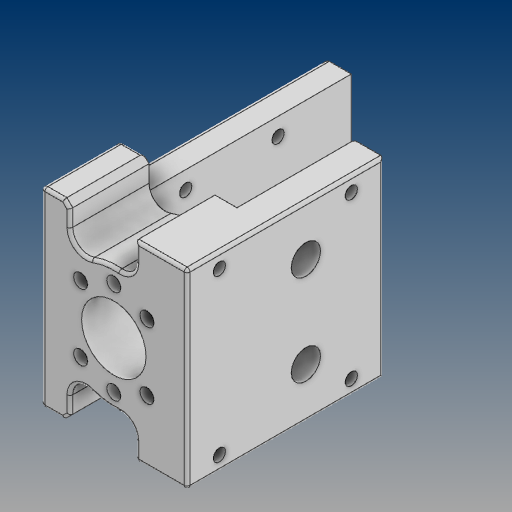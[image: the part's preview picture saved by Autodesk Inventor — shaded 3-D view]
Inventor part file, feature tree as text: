
AUTODESK INVENTOR PART (.ipt)
format: ipt  version: 2021 (Build 250183000, 183)  size: 435,200 bytes
history: native  units: mm
features: extrude x10, sketch x9, projected_geometry x9, reference x6, other x6, fillet x5, plane x1, mirror x1, chamfer x1
ambient origin geometry x8: Origin, YZ Plane, XZ Plane, XY Plane, X Axis, Y Axis, Z Axis, Center Point
bodies: Solid1 (feature_tree)
feature tree (48):
  sketch  "Sketch1"  dims[d0=30.0mm d1=21.0mm]
  plane  "Work Plane1"
  extrude  "Extrusion1"  Depth=21.0mm
  extrude  "Extrusion2"  Depth=30.0mm
  extrude  "Extrusion3"  Depth=15.0mm
  extrude  "Extrusion4"  Depth=10.0mm
  mirror  "Mirror1"
  extrude  "Extrusion5"  Depth=31.0mm
  fillet  "Fillet1"  Radius=5.0mm
  chamfer  "Chamfer1"  Distance=10.0mm
  fillet  "Fillet2"  Radius=10.0mm
  fillet  "Fillet3"  Radius=20.0mm
  sketch  "Sketch7"  dims[d18=4.2mm d19=10.0mm d20=0.0mm d21=10.0mm d22=0.0mm d23=20.0mm]
  extrude  "Extrusion6"  Depth=10.0mm TaperAngle=0.0deg
  extrude  "Extrusion7"  Depth=2.0mm TaperAngle=45.0deg
  extrude  "Extrusion8"  Depth=1.0mm
  fillet  "Fillet4"  Radius=40.0mm
  fillet  "Fillet5"  Radius=45.0mm
  extrude  "Extrusion9"  Depth=5.0mm
  extrude  "Extrusion10"  Depth=1.0mm
  reference  "Reference1"
  sketch  "Sketch3"  dims[d2=30.0mm d3=65.0mm]
  projected_geometry  "Projected Loop2"
  sketch  "Sketch4"  dims[d4=8.0mm d5=15.0mm]
  projected_geometry  "Projected Loop3"
  reference  "Reference2"
  reference  "Reference3"
  sketch  "Sketch5"  dims[d6=10.0mm d7=0.0mm d12=50.0mm]
  reference  "Reference4"
  reference  "Reference5"
  projected_geometry  "Projected Loop4"
  projected_geometry  "Projected Loop5"
  sketch  "Sketch6"  dims[d15=31.5mm d16=31.0mm d17=5.0mm]
  reference  "Reference6"
  projected_geometry  "Projected Loop6"
  projected_geometry  "Projected Loop7"
  sketch  "Sketch8"  dims[d24=10.0mm d25=0.0mm d26=34.5mm d27=0.0mm]
  projected_geometry  "Projected Loop8"
  projected_geometry  "Projected Loop9"
  sketch  "Sketch9"  dims[d28=5.5mm d29=2.0mm d30=2.0mm d31=45.0deg]
  sketch  "Sketch10"  dims[d32=1.5mm d33=5.25mm d34=40.0mm d35=45.0mm d36=5.0mm d37=4.2mm d38=10.0mm d39=0.0mm d40=13.25mm d41=0.0mm d42=30.0mm d43=10.0mm d44=15.75mm d45=0.0mm d46=1.0mm d47=1.0mm d48=21.25mm d49=0.0mm d50=32.0mm d51=1.0mm d52=0.0mm d53=0.0mm]
  projected_geometry  "Projected Loop10"
  other  "<userpath>\Desktop\DO_AN_TOT_NGHIEP_2024\Mechanical\Design_in_3D\Version_1\0012_Bo_truot.iam"
  other  "0012_Bo_truot.iam"
  other  "1204 BALL NUT:1"
  other  "HGR20.ipt:1"
  other  "HGR20C:1"
  other  "HGR20C:3"
